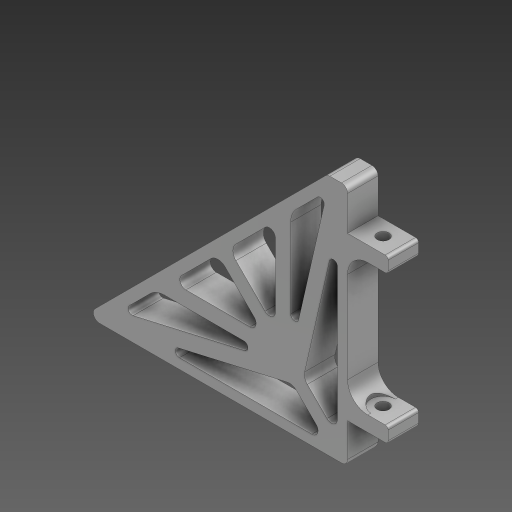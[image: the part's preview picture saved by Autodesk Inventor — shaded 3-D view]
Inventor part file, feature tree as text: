
AUTODESK INVENTOR PART (.ipt)
format: ipt  version: 2024 (Build 280153000, 153)  size: 574,464 bytes
history: native  units: mm
features: fillet x9, sketch x5, extrude x3, hole x2, projected_geometry x1
ambient origin geometry x8: Origin, YZ Plane, XZ Plane, XY Plane, X Axis, Y Axis, Z Axis, Center Point
bodies: Body1 (feature_tree)
feature tree (20):
  extrude  "Extrusion3"  Depth=4.0mm
  fillet  "Fillet2"  Radius=165.0mm
  sketch  "Sketch7"  dims[d43=45.0deg d44=15.0mm d45=0.0mm d46=3.0mm d57=5.0mm d61=7.5mm d63=7.5mm d66=3.75mm d67=7.5mm d70=5.0mm]
  extrude  "Extrusion6"  Depth=15.0mm TaperAngle=0.0deg
  fillet  "Fillet28"  Radius=3.0mm
  fillet  "Fillet29"  Radius=5.0mm
  fillet  "Fillet30"  Radius=7.5mm
  fillet  "Fillet31"  Radius=7.5mm
  fillet  "Fillet32"  Radius=3.75mm
  fillet  "Fillet33"  Radius=7.5mm
  fillet  "Fillet34"  Radius=5.0mm
  hole  "Hole7"  [1 undecoded]
  hole  "Hole8"  [1 undecoded]
  extrude  "Extrusion12"  Depth=7.5mm
  fillet  "Fillet35"  Radius=7.5mm
  sketch  "Sketch1"  dims[d3=30.0mm d41=4.0mm d42=165.0mm]
  sketch  "Sketch16"  dims[d71=0.0mm d72=0.0mm d75=3.75mm]
  sketch  "Sketch18"  dims[d173=20.0mm d174=20.0mm]
  sketch  "Sketch19"  dims[d175=80.0mm d176=7.5mm d177=7.5mm d178=2.0mm d179=10.0mm d180=5.0mm d181=3.0mm d182=5.0mm d183=3.0mm d184=10.0mm d185=5.8mm d186=6.0mm d187=10.0mm d188=5.0mm d189=90.0deg d190=8.0mm d191=20.594885mm d192=7.5mm d196=5.8mm d197=6.0mm d198=4.0mm d199=2.0mm d200=90.0deg d201=8.0mm d202=20.594885mm d203=7.5mm d204=12.0mm d205=10.0mm d206=0.0mm d207=1.5mm d117=0.0mm d118=0.0mm d119=0.0mm d120=0.0mm d125=0.5mm d126=0.872665mm d127=0.5mm d128=0.872665mm d129=0.0mm d130=0.0mm d131=0.0mm d132=0.0mm d208=0.5mm d209=0.872665mm d210=0.5mm d211=0.872665mm]
  projected_geometry  "Project Cut Edges1"
note: 2 required parameter values undecoded (feature->parameter linkage not recoverable at this tier; creation-order binding heuristic only, values carry confidence <= 0.55)
